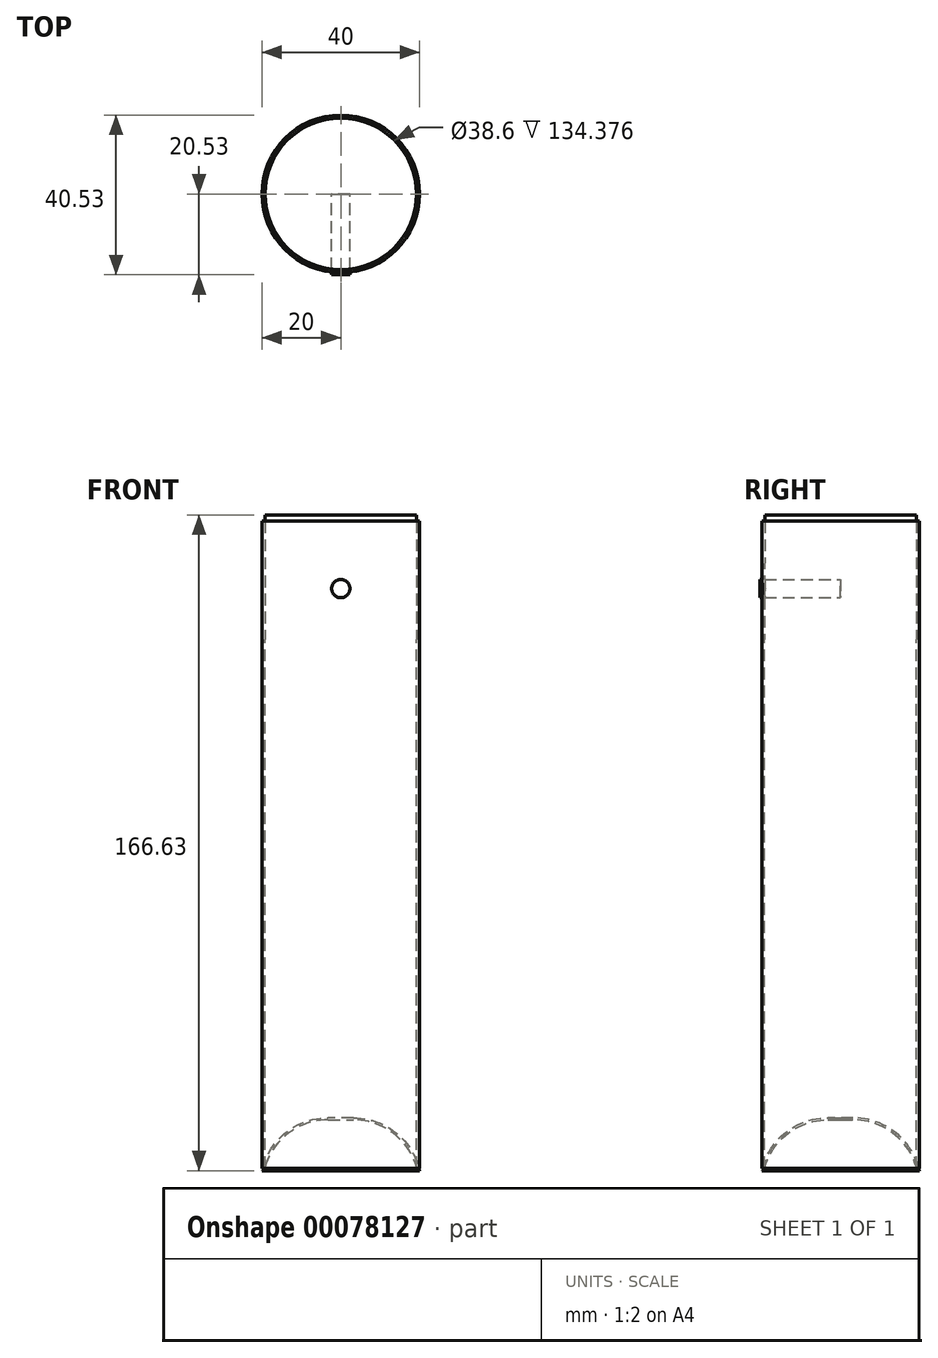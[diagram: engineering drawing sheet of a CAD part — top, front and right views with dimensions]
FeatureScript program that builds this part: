
annotation { "Feature Type Name" : "Feature", "Feature Type Description" : "" }
export const myFeature = defineFeature(function(context is Context, id is Id, definition is map)
    precondition{}
    {
        {
            var Q0;
            Q0=qCreatedBy(makeId("Top.planeOp"),FACE);
            var sketch = newSketch(context, id + "F0", { "sketchPlane" : qUnion([Q0])});
            skCircle(sketch, "E0", {"center": v(0, 0) * mm, "radius": 20 * mm});
            skSolve(sketch);
        }
        {
            var Q0;
            Q0=qCreatedBy(makeId("Top.planeOp"),FACE);
            var sketch = newSketch(context, id + "F1", { "sketchPlane" : qUnion([Q0])});
            skCircle(sketch, "E1", {"center": v(0, 0) * mm, "radius": 20 * mm});
            skSolve(sketch);
        }
        {
            var Q0;
            Q0 = qSketchRegion(id + "F1", true);
            extrude(context, id + "F2", {"entities" : qUnion([Q0]), "depth" : 13.44 * mm});
        }
        {
            var Q0;
            Q0=makeQuery(id+"F2.opExtrude","CAP_FACE",FACE,{"disambiguationData":[OSD([sQuery(id+"F1.wireOp",EDGE,"E1")])],"isStart":false});
            fillet(context, id + "F3", {"entities" : qUnion([Q0]), "radius" : 17.22 * mm, "tangentPropagation" : true, "allowEdgeOverflow" : false});
        }
        {
            var Q0;
            Q0=makeQuery(id+"F2.opExtrude","CAP_FACE",FACE,{"disambiguationData":[OSD([sQuery(id+"F1.wireOp",EDGE,"E1")])],"isStart":true});
            shell(context, id + "F4", {"entities" : qUnion([Q0]), "thickness" : 0.5 * mm});
        }
        {
            var Q0;
            Q0=qCreatedBy(makeId("Front.planeOp"),FACE);
            var sketch = newSketch(context, id + "F5", { "sketchPlane" : qUnion([Q0])});
            skLineSegment(sketch, "E2.0", {"start": v(-20, 0) * mm, "end": v(20, 0) * mm});
            skLineSegment(sketch, "E3", {"start": v(-20, 0) * mm, "end": v(-20, 135) * mm});
            skLineSegment(sketch, "E4", {"start": v(-20, 135) * mm, "end": v(-19.3, 135) * mm});
            skLineSegment(sketch, "E5", {"start": v(-19.3, 135) * mm, "end": v(-19.3, 0.62) * mm});
            skLineSegment(sketch, "E6", {"start": v(-71, 0.62) * mm, "end": v(-19.3, 0.62) * mm});
            skLineSegment(sketch, "E7", {"start": v(-71, 0.62) * mm, "end": v(-71, 0) * mm});
            skSolve(sketch);
        }
        {
            var Q0;
            Q0=qCreatedBy(makeId("Front.planeOp"),FACE);
            var sketch = newSketch(context, id + "F6", { "sketchPlane" : qUnion([Q0])});
            skLineSegment(sketch, "E8.0", {"start": v(-20, 135) * mm, "end": v(-19.3, 135) * mm});
            skLineSegment(sketch, "E9", {"start": v(-20, 135) * mm, "end": v(-20, 165) * mm});
            skLineSegment(sketch, "E10", {"start": v(-20, 165) * mm, "end": v(-19.26, 165) * mm});
            skLineSegment(sketch, "E11", {"start": v(-19.26, 165) * mm, "end": v(-19.3, 135) * mm});
            skSolve(sketch);
        }
        {
            var Q0;
            Q0=makeQuery(id+"F0.imprint","IMPRINT",FACE,{"disambiguationData":[TD([[makeQuery(id+"F0.imprint","IMPRINT",EDGE,{"derivedFrom":sQuery(id+"F0.wireOp",EDGE,"E0")}),1.0]])]});
            extrude(context, id + "F7", {"entities" : qUnion([Q0]), "depth" : 9.8 * mm});
        }
        {
            var Q0;
            {var subQ0=sQuery(id+"F5.wireOp",EDGE,"E3");Q0=makeQuery(id+"F5.imprint","IMPRINT",FACE,{"disambiguationData":[TD([[makeQuery(id+"F5.imprint","IMPRINT",EDGE,{"derivedFrom":subQ0}),-1.0]])]});}
            var Q1;
            Q1=sQuery(id+"F0.wireOp",EDGE,"E0");
            sweep(context, id + "F8", {"profiles" : qUnion([Q0]), "path" : qUnion([Q1])});
        }
        {
            var Q0;
            Q0=makeQuery(id+"F6.imprint","IMPRINT",FACE,{"disambiguationData":[TD([[makeQuery(id+"F6.imprint","IMPRINT",EDGE,{"derivedFrom":sQuery(id+"F6.wireOp",EDGE,"E8.0")}),1.0]])]});
            var Q1;
            Q1=makeQuery(id+"F8.opSweep","SWEPT_EDGE",EDGE,{"disambiguationData":[OSD([sQuery(id+"F0.wireOp",EDGE,"E0"),sQuery(id+"F5.wireOp",EDGE,"E3"),sQuery(id+"F5.wireOp",EDGE,"E4")])]});
            sweep(context, id + "F9", {"operationType" : NewBodyOperationType.ADD, "profiles" : qUnion([Q0]), "path" : qUnion([Q1])});
        }
        {
            var Q0;
            Q0=makeQuery(id+"F7.opExtrude","SWEPT_BODY",BODY,{"disambiguationData":[OSD([sQuery(id+"F0.wireOp",EDGE,"E0")])]});
            deleteBodies(context, id + "F10", {"entities" : qUnion([Q0])});
        }
        {
            var Q0;
            Q0=qCreatedBy(makeId("Front.planeOp"),FACE);
            var sketch = newSketch(context, id + "F11", { "sketchPlane" : qUnion([Q0])});
            skCircle(sketch, "E12", {"center": v(0, 147.9) * mm, "radius": 2.33 * mm});
            skSolve(sketch);
        }
        {
            var Q0;
            Q0=makeQuery(id+"F11.imprint","IMPRINT",FACE,{"disambiguationData":[TD([[makeQuery(id+"F11.imprint","IMPRINT",EDGE,{"derivedFrom":sQuery(id+"F11.wireOp",EDGE,"E12")}),1.0]])]});
            extrude(context, id + "F12", {"entities" : qUnion([Q0]), "operationType" : NewBodyOperationType.ADD, "depth" : 20.53 * mm});
        }
        {
            var Q0;
            Q0=makeQuery(id+"F9.opSweep","SWEPT_FACE",FACE,{"disambiguationData":[OSD([sQuery(id+"F0.wireOp",EDGE,"E0"),sQuery(id+"F5.wireOp",EDGE,"E3"),sQuery(id+"F5.wireOp",EDGE,"E4"),sQuery(id+"F6.wireOp",EDGE,"E10")])]});
            var sketch = newSketch(context, id + "F13", { "sketchPlane" : qUnion([Q0])});
            skCircle(sketch, "E13.0", {"center": v(0, 0) * mm, "radius": 20 * mm});
            skCircle(sketch, "E14", {"center": v(0.09, -0.2) * mm, "radius": 20.08 * mm});
            skPoint(sketch, "E14.first.point", {"position": v(-19.94, -1.54) * mm});
            skPoint(sketch, "E14.second.point", {"position": v(20.08, 1.64) * mm});
            skPoint(sketch, "E14.third.point", {"position": v(14.16, 14.13) * mm});
            skSolve(sketch);
        }
        {
            var Q0;
            Q0=makeQuery(id+"F13.imprint","IMPRINT",FACE,{"disambiguationData":[TD([[makeQuery(id+"F13.imprint","IMPRINT",EDGE,{"derivedFrom":makeQuery(id+"F9.opSweep","SWEPT_EDGE",EDGE,{"disambiguationData":[OSD([sQuery(id+"F0.wireOp",EDGE,"E0"),sQuery(id+"F5.wireOp",EDGE,"E3"),sQuery(id+"F5.wireOp",EDGE,"E4"),sQuery(id+"F6.wireOp",EDGE,"E10"),sQuery(id+"F6.wireOp",EDGE,"E11")])]})}),1.0]])]});
            extrude(context, id + "F14", {"entities" : qUnion([Q0]), "operationType" : NewBodyOperationType.ADD, "depth" : 1.63 * mm});
        }
    });
